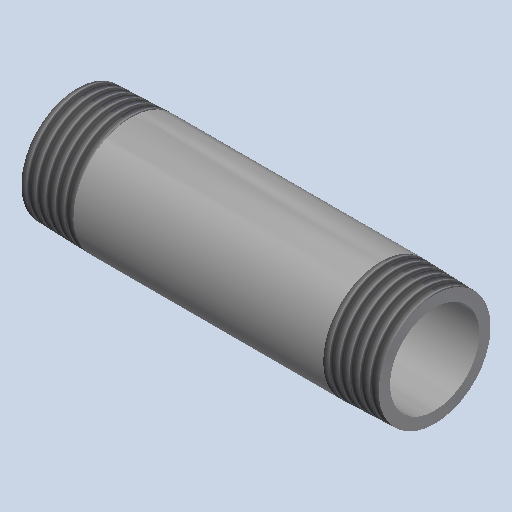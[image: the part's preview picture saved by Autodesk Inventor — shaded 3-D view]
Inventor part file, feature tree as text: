
AUTODESK INVENTOR PART (.ipt)
format: ipt  version: 2025 (Build 290162000, 162)  size: 232,960 bytes
history: native  units: mm (DEFAULTED — no unit token found)
features: other x8, revolve x1
ambient origin geometry x8: Origin, YZ Plane, XZ Plane, XY Plane, X Axis, Y Axis, Z Axis, Center Point
bodies: Solid1 (feature_tree)
feature tree (9):
  revolve  "Revolution1"  [1 undecoded]
  other  "Work Axis1"
  other  "Work Point5"
  other  "Work Axis2"
  other  "Work Point6"
  other  "Work Axis3"
  other  "Work Axis4"
  other  "Work Point7"
  other  "Work Point8"
note: 1 required parameter value undecoded (feature->parameter linkage not recoverable at this tier; creation-order binding heuristic only, values carry confidence <= 0.55)
